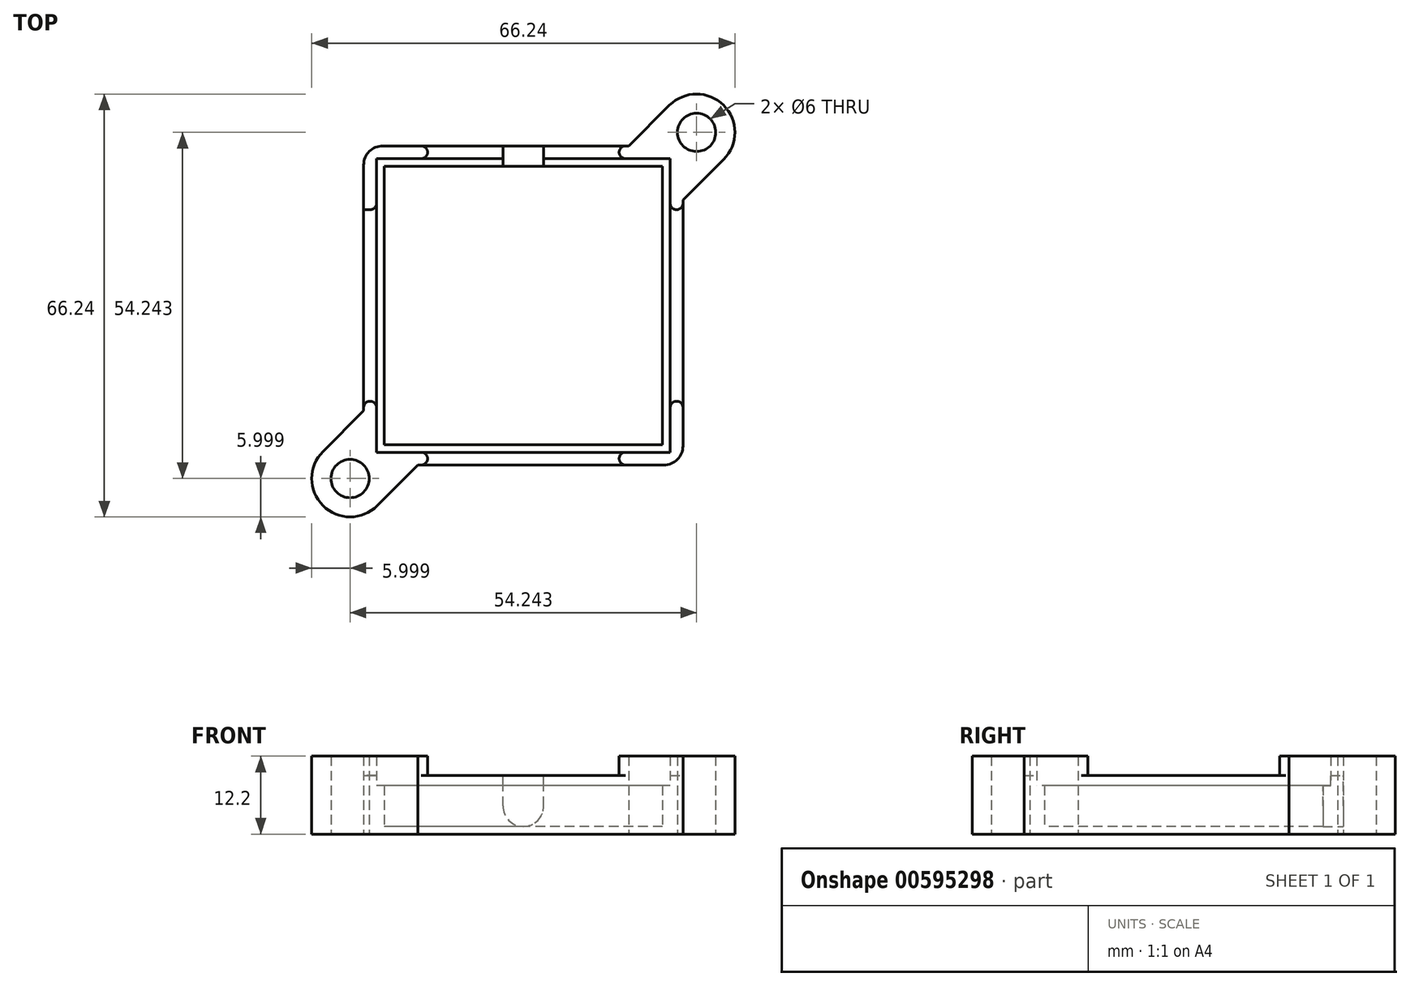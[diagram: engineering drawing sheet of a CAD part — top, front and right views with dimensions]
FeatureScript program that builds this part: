
annotation { "Feature Type Name" : "Feature", "Feature Type Description" : "" }
export const myFeature = defineFeature(function(context is Context, id is Id, definition is map)
    precondition{}
    {
        {
            var Q0;
            Q0=qCreatedBy(makeId("Top.planeOp"),FACE);
            var sketch = newSketch(context, id + "F0", { "sketchPlane" : qUnion([Q0])});
            skLineSegment(sketch, "E0.bottom", {"start": v(16.51, 25) * mm, "end": v(-25, 25) * mm});
            skLineSegment(sketch, "E0.top", {"start": v(25, -25) * mm, "end": v(-16.51, -25) * mm});
            skLineSegment(sketch, "E0.left", {"start": v(25, 16.51) * mm, "end": v(25, -25) * mm});
            skLineSegment(sketch, "E0.right", {"start": v(-25, 25) * mm, "end": v(-25, -16.51) * mm});
            skPoint(sketch, "E0.middle", {"position": v(0, 0) * mm});
            skLineSegment(sketch, "E1", {"start": v(0, 0) * mm, "end": v(27.12, 27.12) * mm, "construction": true});
            skArc(sketch, "E2", {"start": v(31.36, 22.88) * mm, "mid": v(31.36, 31.36) * mm, "end": v(22.88, 31.36) * mm});
            skLineSegment(sketch, "E3", {"start": v(31.36, 22.88) * mm, "end": v(25, 16.51) * mm});
            skLineSegment(sketch, "E4", {"start": v(22.88, 31.36) * mm, "end": v(16.51, 25) * mm});
            skPoint(sketch, "E5.orphan", {"position": v(25, 25) * mm});
            skLineSegment(sketch, "E6", {"start": v(16.51, 25) * mm, "end": v(25, 25) * mm, "construction": true});
            skLineSegment(sketch, "E7", {"start": v(25, 16.51) * mm, "end": v(25, 25) * mm, "construction": true});
            skCircle(sketch, "E8", {"center": v(27.12, 27.12) * mm, "radius": 3 * mm});
            skLineSegment(sketch, "E9", {"start": v(-25, 25) * mm, "end": v(25, -25) * mm, "construction": true});
            skArc(sketch, "E10.MirrorCS", {"start": v(-22.88, -31.36) * mm, "mid": v(-31.36, -31.36) * mm, "end": v(-31.36, -22.88) * mm});
            skLineSegment(sketch, "E11.MirrorCS", {"start": v(-31.36, -22.88) * mm, "end": v(-25, -16.51) * mm});
            skLineSegment(sketch, "E12.MirrorCS", {"start": v(-22.88, -31.36) * mm, "end": v(-16.51, -25) * mm});
            skCircle(sketch, "E13.MirrorC", {"center": v(-27.12, -27.12) * mm, "radius": 3 * mm});
            skLineSegment(sketch, "E14", {"start": v(-25, -16.51) * mm, "end": v(-25, -25) * mm, "construction": true});
            skLineSegment(sketch, "E15", {"start": v(-16.51, -25) * mm, "end": v(-25, -25) * mm, "construction": true});
            skSolve(sketch);
        }
        {
            var Q0;
            Q0=makeQuery(id+"F0.imprint","IMPRINT",FACE,{"disambiguationData":[TD([[makeQuery(id+"F0.imprint","IMPRINT",EDGE,{"derivedFrom":sQuery(id+"F0.wireOp",EDGE,"E0.bottom")}),1.0]])]});
            extrude(context, id + "F1", {"entities" : qUnion([Q0]), "depth" : 1.2 * mm, "offsetDistance" : 25 * mm});
        }
        {
            var Q0;
            Q0=makeQuery(id+"F1.opExtrude","CAP_FACE",FACE,{"disambiguationData":[OSD([sQuery(id+"F0.wireOp",EDGE,"E0.bottom"),sQuery(id+"F0.wireOp",EDGE,"E0.top"),sQuery(id+"F0.wireOp",EDGE,"E0.left"),sQuery(id+"F0.wireOp",EDGE,"E0.right"),sQuery(id+"F0.wireOp",EDGE,"E2"),sQuery(id+"F0.wireOp",EDGE,"E3"),sQuery(id+"F0.wireOp",EDGE,"E4"),sQuery(id+"F0.wireOp",EDGE,"E8"),sQuery(id+"F0.wireOp",EDGE,"E10.MirrorCS"),sQuery(id+"F0.wireOp",EDGE,"E11.MirrorCS"),sQuery(id+"F0.wireOp",EDGE,"E12.MirrorCS"),sQuery(id+"F0.wireOp",EDGE,"E13.MirrorC")])],"isStart":false});
            var sketch = newSketch(context, id + "F2", { "sketchPlane" : qUnion([Q0])});
            skLineSegment(sketch, "E16.0.0", {"start": v(25, -25) * mm, "end": v(25, 16.51) * mm});
            skLineSegment(sketch, "E16.0.1", {"start": v(25, 16.51) * mm, "end": v(31.36, 22.88) * mm});
            skArc(sketch, "E16.0.2", {"start": v(31.36, 22.88) * mm, "mid": v(31.36, 31.36) * mm, "end": v(22.88, 31.36) * mm});
            skLineSegment(sketch, "E16.0.3", {"start": v(22.88, 31.36) * mm, "end": v(16.51, 25) * mm});
            skLineSegment(sketch, "E16.0.4", {"start": v(16.51, 25) * mm, "end": v(-25, 25) * mm});
            skLineSegment(sketch, "E16.0.5", {"start": v(-25, 25) * mm, "end": v(-25, -16.51) * mm});
            skLineSegment(sketch, "E16.0.6", {"start": v(-25, -16.51) * mm, "end": v(-31.36, -22.88) * mm});
            skArc(sketch, "E16.0.7", {"start": v(-31.36, -22.88) * mm, "mid": v(-31.36, -31.36) * mm, "end": v(-22.88, -31.36) * mm});
            skLineSegment(sketch, "E16.0.8", {"start": v(-22.88, -31.36) * mm, "end": v(-16.51, -25) * mm});
            skLineSegment(sketch, "E16.0.9", {"start": v(-16.51, -25) * mm, "end": v(25, -25) * mm});
            skLineSegment(sketch, "E17.bottom", {"start": v(21.8, 21.8) * mm, "end": v(-21.8, 21.8) * mm});
            skLineSegment(sketch, "E17.top", {"start": v(21.8, -21.8) * mm, "end": v(-21.8, -21.8) * mm});
            skLineSegment(sketch, "E17.left", {"start": v(21.8, 21.8) * mm, "end": v(21.8, -21.8) * mm});
            skLineSegment(sketch, "E17.right", {"start": v(-21.8, 21.8) * mm, "end": v(-21.8, -21.8) * mm});
            skPoint(sketch, "E17.middle", {"position": v(0, 0) * mm});
            skSolve(sketch);
        }
        {
            var Q0;
            Q0=makeQuery(id+"F2.imprint","IMPRINT",FACE,{"disambiguationData":[TD([[makeQuery(id+"F2.imprint","IMPRINT",EDGE,{"derivedFrom":sQuery(id+"F2.wireOp",EDGE,"E16.0.0")}),-1.0]])]});
            extrude(context, id + "F3", {"entities" : qUnion([Q0]), "operationType" : NewBodyOperationType.ADD, "depth" : 6.4 * mm, "offsetDistance" : 25 * mm});
        }
        {
            var Q0;
            Q0=makeQuery(id+"F3.opExtrude","CAP_FACE",FACE,{"disambiguationData":[OSD([sQuery(id+"F0.wireOp",EDGE,"E8"),sQuery(id+"F0.wireOp",EDGE,"E13.MirrorC"),sQuery(id+"F2.wireOp",EDGE,"E16.0.0"),sQuery(id+"F2.wireOp",EDGE,"E16.0.1"),sQuery(id+"F2.wireOp",EDGE,"E16.0.2"),sQuery(id+"F2.wireOp",EDGE,"E16.0.3"),sQuery(id+"F2.wireOp",EDGE,"E16.0.4"),sQuery(id+"F2.wireOp",EDGE,"E16.0.5"),sQuery(id+"F2.wireOp",EDGE,"E16.0.6"),sQuery(id+"F2.wireOp",EDGE,"E16.0.7"),sQuery(id+"F2.wireOp",EDGE,"E16.0.8"),sQuery(id+"F2.wireOp",EDGE,"E16.0.9"),sQuery(id+"F2.wireOp",EDGE,"E17.bottom"),sQuery(id+"F2.wireOp",EDGE,"E17.top"),sQuery(id+"F2.wireOp",EDGE,"E17.left"),sQuery(id+"F2.wireOp",EDGE,"E17.right")])],"isStart":false});
            var sketch = newSketch(context, id + "F4", { "sketchPlane" : qUnion([Q0])});
            skLineSegment(sketch, "E18.0.0", {"start": v(25, -25) * mm, "end": v(25, 16.51) * mm});
            skLineSegment(sketch, "E18.0.1", {"start": v(25, 16.51) * mm, "end": v(31.36, 22.88) * mm});
            skArc(sketch, "E18.0.2", {"start": v(31.36, 22.88) * mm, "mid": v(31.36, 31.36) * mm, "end": v(22.88, 31.36) * mm});
            skLineSegment(sketch, "E18.0.3", {"start": v(22.88, 31.36) * mm, "end": v(16.51, 25) * mm});
            skLineSegment(sketch, "E18.0.4", {"start": v(16.51, 25) * mm, "end": v(-25, 25) * mm});
            skLineSegment(sketch, "E18.0.5", {"start": v(-25, 25) * mm, "end": v(-25, -16.51) * mm});
            skLineSegment(sketch, "E18.0.6", {"start": v(-25, -16.51) * mm, "end": v(-31.36, -22.88) * mm});
            skArc(sketch, "E18.0.7", {"start": v(-31.36, -22.88) * mm, "mid": v(-31.36, -31.36) * mm, "end": v(-22.88, -31.36) * mm});
            skLineSegment(sketch, "E18.0.8", {"start": v(-22.88, -31.36) * mm, "end": v(-16.51, -25) * mm});
            skLineSegment(sketch, "E18.0.9", {"start": v(-16.51, -25) * mm, "end": v(25, -25) * mm});
            skLineSegment(sketch, "E19.0", {"start": v(-23, 23) * mm, "end": v(-23, -23) * mm});
            skLineSegment(sketch, "E19.1", {"start": v(23, 23) * mm, "end": v(-23, 23) * mm});
            skLineSegment(sketch, "E19.2", {"start": v(23, 23) * mm, "end": v(23, -23) * mm});
            skLineSegment(sketch, "E19.3", {"start": v(23, -23) * mm, "end": v(-23, -23) * mm});
            skSolve(sketch);
        }
        {
            var Q0;
            Q0=makeQuery(id+"F4.imprint","IMPRINT",FACE,{"disambiguationData":[TD([[makeQuery(id+"F4.imprint","IMPRINT",EDGE,{"derivedFrom":sQuery(id+"F4.wireOp",EDGE,"E18.0.0")}),-1.0]])]});
            extrude(context, id + "F5", {"entities" : qUnion([Q0]), "operationType" : NewBodyOperationType.ADD, "depth" : 1.6 * mm, "offsetDistance" : 25 * mm});
        }
        {
            var Q0;
            Q0=makeQuery(id+"F5.opExtrude","CAP_FACE",FACE,{"disambiguationData":[OSD([sQuery(id+"F0.wireOp",EDGE,"E8"),sQuery(id+"F0.wireOp",EDGE,"E13.MirrorC"),sQuery(id+"F4.wireOp",EDGE,"E18.0.0"),sQuery(id+"F4.wireOp",EDGE,"E18.0.1"),sQuery(id+"F4.wireOp",EDGE,"E18.0.2"),sQuery(id+"F4.wireOp",EDGE,"E18.0.3"),sQuery(id+"F4.wireOp",EDGE,"E18.0.4"),sQuery(id+"F4.wireOp",EDGE,"E18.0.5"),sQuery(id+"F4.wireOp",EDGE,"E18.0.6"),sQuery(id+"F4.wireOp",EDGE,"E18.0.7"),sQuery(id+"F4.wireOp",EDGE,"E18.0.8"),sQuery(id+"F4.wireOp",EDGE,"E18.0.9"),sQuery(id+"F4.wireOp",EDGE,"E19.0"),sQuery(id+"F4.wireOp",EDGE,"E19.1"),sQuery(id+"F4.wireOp",EDGE,"E19.2"),sQuery(id+"F4.wireOp",EDGE,"E19.3")])],"isStart":false});
            var sketch = newSketch(context, id + "F6", { "sketchPlane" : qUnion([Q0])});
            skLineSegment(sketch, "E20.0.0", {"start": v(25, -25) * mm, "end": v(25, -15) * mm});
            skLineSegment(sketch, "E20.0.1", {"start": v(25, 16.51) * mm, "end": v(31.36, 22.88) * mm});
            skArc(sketch, "E20.0.2", {"start": v(31.36, 22.88) * mm, "mid": v(31.36, 31.36) * mm, "end": v(22.88, 31.36) * mm});
            skLineSegment(sketch, "E20.0.3", {"start": v(22.88, 31.36) * mm, "end": v(16.51, 25) * mm});
            skLineSegment(sketch, "E20.0.4", {"start": v(16.51, 25) * mm, "end": v(15, 25) * mm});
            skLineSegment(sketch, "E20.0.5", {"start": v(-25, 25) * mm, "end": v(-25, 15) * mm});
            skLineSegment(sketch, "E20.0.6", {"start": v(-25, -16.51) * mm, "end": v(-31.36, -22.88) * mm});
            skArc(sketch, "E20.0.7", {"start": v(-31.36, -22.88) * mm, "mid": v(-31.36, -31.36) * mm, "end": v(-22.88, -31.36) * mm});
            skLineSegment(sketch, "E20.0.8", {"start": v(-22.88, -31.36) * mm, "end": v(-16.51, -25) * mm});
            skLineSegment(sketch, "E20.0.9", {"start": v(-16.51, -25) * mm, "end": v(-15, -25) * mm});
            skLineSegment(sketch, "E21.bottom", {"start": v(23, 23) * mm, "end": v(15, 23) * mm});
            skLineSegment(sketch, "E21.top", {"start": v(23, -23) * mm, "end": v(15, -23) * mm});
            skLineSegment(sketch, "E21.left", {"start": v(23, 23) * mm, "end": v(23, 15) * mm});
            skLineSegment(sketch, "E21.right", {"start": v(-23, 23) * mm, "end": v(-23, 15) * mm});
            skPoint(sketch, "E21.middle", {"position": v(0, 0) * mm});
            skLineSegment(sketch, "E22", {"start": v(-15, 25) * mm, "end": v(-15, 23) * mm});
            skLineSegment(sketch, "E23", {"start": v(-15, -23) * mm, "end": v(-15, -25) * mm});
            skLineSegment(sketch, "E24", {"start": v(-25, 15) * mm, "end": v(-23, 15) * mm});
            skLineSegment(sketch, "E25", {"start": v(23, 15) * mm, "end": v(25, 15) * mm});
            skLineSegment(sketch, "E26.MirrorCS", {"start": v(15, 25) * mm, "end": v(15, 23) * mm});
            skLineSegment(sketch, "E27.MirrorCS", {"start": v(15, -23) * mm, "end": v(15, -25) * mm});
            skLineSegment(sketch, "E28.MirrorCS", {"start": v(-25, -15) * mm, "end": v(-23, -15) * mm});
            skLineSegment(sketch, "E29.MirrorCS", {"start": v(23, -15) * mm, "end": v(25, -15) * mm});
            skLineSegment(sketch, "E30.trimOffspring", {"start": v(-15, 25) * mm, "end": v(-25, 25) * mm});
            skLineSegment(sketch, "E31.trimOffspring", {"start": v(-15, 23) * mm, "end": v(-23, 23) * mm});
            skLineSegment(sketch, "E32.trimOffspring", {"start": v(23, -15) * mm, "end": v(23, -23) * mm});
            skLineSegment(sketch, "E33.trimOffspring", {"start": v(25, 15) * mm, "end": v(25, 16.51) * mm});
            skLineSegment(sketch, "E34.trimOffspring", {"start": v(-15, -23) * mm, "end": v(-23, -23) * mm});
            skLineSegment(sketch, "E35.trimOffspring", {"start": v(15, -25) * mm, "end": v(25, -25) * mm});
            skLineSegment(sketch, "E36.trimOffspring", {"start": v(-25, -15) * mm, "end": v(-25, -16.51) * mm});
            skLineSegment(sketch, "E37.trimOffspring", {"start": v(-23, -15) * mm, "end": v(-23, -23) * mm});
            skCircle(sketch, "E38.0", {"center": v(-27.12, -27.12) * mm, "radius": 3 * mm});
            skCircle(sketch, "E39.0", {"center": v(27.12, 27.12) * mm, "radius": 3 * mm});
            skSolve(sketch);
        }
        {
            var Q0;
            Q0 = qSketchRegion(id + "F6", true);
            extrude(context, id + "F7", {"entities" : qUnion([Q0]), "operationType" : NewBodyOperationType.ADD, "depth" : 3 * mm, "offsetDistance" : 25 * mm});
        }
        {
            var Q0;
            Q0=makeQuery(id+"F7.boolean.opBoolean","MERGE",FACE,{"derivedFrom":[makeQuery(id+"F5.boolean.opBoolean","MERGE",FACE,{"derivedFrom":[makeQuery(id+"F3.boolean.opBoolean","MERGE",FACE,{"derivedFrom":[makeQuery(id+"F1.opExtrude","SWEPT_FACE",FACE,{"disambiguationData":[OSD([sQuery(id+"F0.wireOp",EDGE,"E0.bottom")])]}),makeQuery(id+"F3.opExtrude","SWEPT_FACE",FACE,{"disambiguationData":[OSD([sQuery(id+"F2.wireOp",EDGE,"E16.0.4")])]})]}),makeQuery(id+"F5.opExtrude","SWEPT_FACE",FACE,{"disambiguationData":[OSD([sQuery(id+"F4.wireOp",EDGE,"E18.0.4")])]})]}),makeQuery(id+"F7.opExtrude","SWEPT_FACE",FACE,{"disambiguationData":[OSD([sQuery(id+"F6.wireOp",EDGE,"E20.0.4")])]}),makeQuery(id+"F7.opExtrude","SWEPT_FACE",FACE,{"disambiguationData":[OSD([sQuery(id+"F6.wireOp",EDGE,"E30.trimOffspring")])]})]});
            var sketch = newSketch(context, id + "F8", { "sketchPlane" : qUnion([Q0])});
            skLineSegment(sketch, "E40.0", {"start": v(-15, 9.2) * mm, "end": v(-3.2, 9.2) * mm, "construction": true});
            skLineSegment(sketch, "E41.0", {"start": v(-21.8, 1.2) * mm, "end": v(21.8, 1.2) * mm, "construction": true});
            skArc(sketch, "E42", {"start": v(-3.2, 4.4) * mm, "mid": v(0, 1.2) * mm, "end": v(3.2, 4.4) * mm});
            skPoint(sketch, "E42.centerSnap0", {"position": v(0, 9.2) * mm});
            skLineSegment(sketch, "E43", {"start": v(-3.2, 4.4) * mm, "end": v(-3.2, 9.2) * mm});
            skLineSegment(sketch, "E44", {"start": v(3.2, 4.4) * mm, "end": v(3.2, 9.2) * mm});
            skLineSegment(sketch, "E45", {"start": v(-3.2, 9.2) * mm, "end": v(-3.2, 9.2) * mm});
            skLineSegment(sketch, "E46", {"start": v(3.2, 9.2) * mm, "end": v(15, 9.2) * mm, "construction": true});
            skLineSegment(sketch, "E47", {"start": v(-3.2, 9.2) * mm, "end": v(3.2, 9.2) * mm});
            skLineSegment(sketch, "E48.0", {"start": v(-21.8, 7.6) * mm, "end": v(21.8, 7.6) * mm, "construction": true});
            skSolve(sketch);
        }
        {
            var Q0;
            Q0 = qSketchRegion(id + "F8", true);
            extrude(context, id + "F9", {"entities" : qUnion([Q0]), "operationType" : NewBodyOperationType.REMOVE, "endBound" : BoundingType.UP_TO_NEXT, "oppositeDirection" : true, "depth" : 25 * mm, "offsetDistance" : 25 * mm});
        }
        {
            var Q0;
            Q0=makeQuery(id+"F7.opExtrude","SWEPT_EDGE",EDGE,{"disambiguationData":[OSD([sQuery(id+"F4.wireOp",EDGE,"E18.0.0"),sQuery(id+"F6.wireOp",EDGE,"E20.0.0"),sQuery(id+"F6.wireOp",EDGE,"E29.MirrorCS")])]});
            var Q1;
            Q1=makeQuery(id+"F7.opExtrude","SWEPT_EDGE",EDGE,{"disambiguationData":[OSD([sQuery(id+"F4.wireOp",EDGE,"E19.2"),sQuery(id+"F6.wireOp",EDGE,"E29.MirrorCS"),sQuery(id+"F6.wireOp",EDGE,"E32.trimOffspring")])]});
            var Q2;
            Q2=makeQuery(id+"F7.opExtrude","SWEPT_EDGE",EDGE,{"disambiguationData":[OSD([sQuery(id+"F4.wireOp",EDGE,"E18.0.9"),sQuery(id+"F6.wireOp",EDGE,"E27.MirrorCS"),sQuery(id+"F6.wireOp",EDGE,"E35.trimOffspring")])]});
            var Q3;
            Q3=makeQuery(id+"F7.opExtrude","SWEPT_EDGE",EDGE,{"disambiguationData":[OSD([sQuery(id+"F4.wireOp",EDGE,"E19.3"),sQuery(id+"F6.wireOp",EDGE,"E21.top"),sQuery(id+"F6.wireOp",EDGE,"E27.MirrorCS")])]});
            var Q4;
            Q4=makeQuery(id+"F7.opExtrude","SWEPT_EDGE",EDGE,{"disambiguationData":[OSD([sQuery(id+"F4.wireOp",EDGE,"E18.0.9"),sQuery(id+"F6.wireOp",EDGE,"E20.0.9"),sQuery(id+"F6.wireOp",EDGE,"E23")])]});
            var Q5;
            Q5=makeQuery(id+"F7.opExtrude","SWEPT_EDGE",EDGE,{"disambiguationData":[OSD([sQuery(id+"F4.wireOp",EDGE,"E19.3"),sQuery(id+"F6.wireOp",EDGE,"E23"),sQuery(id+"F6.wireOp",EDGE,"E34.trimOffspring")])]});
            var Q6;
            Q6=makeQuery(id+"F7.opExtrude","SWEPT_EDGE",EDGE,{"disambiguationData":[OSD([sQuery(id+"F4.wireOp",EDGE,"E19.0"),sQuery(id+"F6.wireOp",EDGE,"E28.MirrorCS"),sQuery(id+"F6.wireOp",EDGE,"E37.trimOffspring")])]});
            var Q7;
            Q7=makeQuery(id+"F7.opExtrude","SWEPT_EDGE",EDGE,{"disambiguationData":[OSD([sQuery(id+"F4.wireOp",EDGE,"E19.0"),sQuery(id+"F6.wireOp",EDGE,"E21.right"),sQuery(id+"F6.wireOp",EDGE,"E24")])]});
            var Q8;
            Q8=makeQuery(id+"F7.opExtrude","SWEPT_EDGE",EDGE,{"disambiguationData":[OSD([sQuery(id+"F4.wireOp",EDGE,"E18.0.5"),sQuery(id+"F6.wireOp",EDGE,"E28.MirrorCS"),sQuery(id+"F6.wireOp",EDGE,"E36.trimOffspring")])]});
            var Q9;
            Q9=makeQuery(id+"F7.opExtrude","SWEPT_EDGE",EDGE,{"disambiguationData":[OSD([sQuery(id+"F4.wireOp",EDGE,"E19.1"),sQuery(id+"F6.wireOp",EDGE,"E22"),sQuery(id+"F6.wireOp",EDGE,"E31.trimOffspring")])]});
            var Q10;
            Q10=makeQuery(id+"F7.opExtrude","SWEPT_EDGE",EDGE,{"disambiguationData":[OSD([sQuery(id+"F4.wireOp",EDGE,"E18.0.4"),sQuery(id+"F6.wireOp",EDGE,"E22"),sQuery(id+"F6.wireOp",EDGE,"E30.trimOffspring")])]});
            var Q11;
            Q11=makeQuery(id+"F7.opExtrude","SWEPT_EDGE",EDGE,{"disambiguationData":[OSD([sQuery(id+"F4.wireOp",EDGE,"E19.1"),sQuery(id+"F6.wireOp",EDGE,"E21.bottom"),sQuery(id+"F6.wireOp",EDGE,"E26.MirrorCS")])]});
            var Q12;
            Q12=makeQuery(id+"F7.opExtrude","SWEPT_EDGE",EDGE,{"disambiguationData":[OSD([sQuery(id+"F4.wireOp",EDGE,"E18.0.4"),sQuery(id+"F6.wireOp",EDGE,"E20.0.4"),sQuery(id+"F6.wireOp",EDGE,"E26.MirrorCS")])]});
            var Q13;
            Q13=makeQuery(id+"F7.opExtrude","SWEPT_EDGE",EDGE,{"disambiguationData":[OSD([sQuery(id+"F4.wireOp",EDGE,"E19.2"),sQuery(id+"F6.wireOp",EDGE,"E21.left"),sQuery(id+"F6.wireOp",EDGE,"E25")])]});
            var Q14;
            Q14=makeQuery(id+"F7.opExtrude","SWEPT_EDGE",EDGE,{"disambiguationData":[OSD([sQuery(id+"F4.wireOp",EDGE,"E18.0.0"),sQuery(id+"F6.wireOp",EDGE,"E25"),sQuery(id+"F6.wireOp",EDGE,"E33.trimOffspring")])]});
            fillet(context, id + "F10", {"entities" : qUnion([Q0, Q1, Q2, Q3, Q4, Q5, Q6, Q7, Q8, Q9, Q10, Q11, Q12, Q13, Q14]), "radius" : 1 * mm, "tangentPropagation" : true, "allowEdgeOverflow" : false});
        }
        {
            var Q0;
            Q0=makeQuery(id+"F7.boolean.opBoolean","MERGE",EDGE,{"derivedFrom":[makeQuery(id+"F5.boolean.opBoolean","MERGE",EDGE,{"derivedFrom":[makeQuery(id+"F3.boolean.opBoolean","MERGE",EDGE,{"derivedFrom":[makeQuery(id+"F1.opExtrude","SWEPT_EDGE",EDGE,{"disambiguationData":[OSD([sQuery(id+"F0.wireOp",EDGE,"E0.bottom"),sQuery(id+"F0.wireOp",EDGE,"E0.right")])]}),makeQuery(id+"F3.opExtrude","SWEPT_EDGE",EDGE,{"disambiguationData":[OSD([sQuery(id+"F2.wireOp",EDGE,"E16.0.4"),sQuery(id+"F2.wireOp",EDGE,"E16.0.5")])]})]}),makeQuery(id+"F5.opExtrude","SWEPT_EDGE",EDGE,{"disambiguationData":[OSD([sQuery(id+"F4.wireOp",EDGE,"E18.0.4"),sQuery(id+"F4.wireOp",EDGE,"E18.0.5")])]})]}),makeQuery(id+"F7.opExtrude","SWEPT_EDGE",EDGE,{"disambiguationData":[OSD([sQuery(id+"F6.wireOp",EDGE,"E20.0.5"),sQuery(id+"F6.wireOp",EDGE,"E30.trimOffspring")])]})]});
            var Q1;
            Q1=makeQuery(id+"F7.boolean.opBoolean","MERGE",EDGE,{"derivedFrom":[makeQuery(id+"F5.boolean.opBoolean","MERGE",EDGE,{"derivedFrom":[makeQuery(id+"F3.boolean.opBoolean","MERGE",EDGE,{"derivedFrom":[makeQuery(id+"F1.opExtrude","SWEPT_EDGE",EDGE,{"disambiguationData":[OSD([sQuery(id+"F0.wireOp",EDGE,"E0.top"),sQuery(id+"F0.wireOp",EDGE,"E0.left")])]}),makeQuery(id+"F3.opExtrude","SWEPT_EDGE",EDGE,{"disambiguationData":[OSD([sQuery(id+"F2.wireOp",EDGE,"E16.0.0"),sQuery(id+"F2.wireOp",EDGE,"E16.0.9")])]})]}),makeQuery(id+"F5.opExtrude","SWEPT_EDGE",EDGE,{"disambiguationData":[OSD([sQuery(id+"F4.wireOp",EDGE,"E18.0.0"),sQuery(id+"F4.wireOp",EDGE,"E18.0.9")])]})]}),makeQuery(id+"F7.opExtrude","SWEPT_EDGE",EDGE,{"disambiguationData":[OSD([sQuery(id+"F6.wireOp",EDGE,"E20.0.0"),sQuery(id+"F6.wireOp",EDGE,"E35.trimOffspring")])]})]});
            fillet(context, id + "F11", {"entities" : qUnion([Q0, Q1]), "radius" : 3 * mm, "tangentPropagation" : true, "allowEdgeOverflow" : false});
        }
    });
